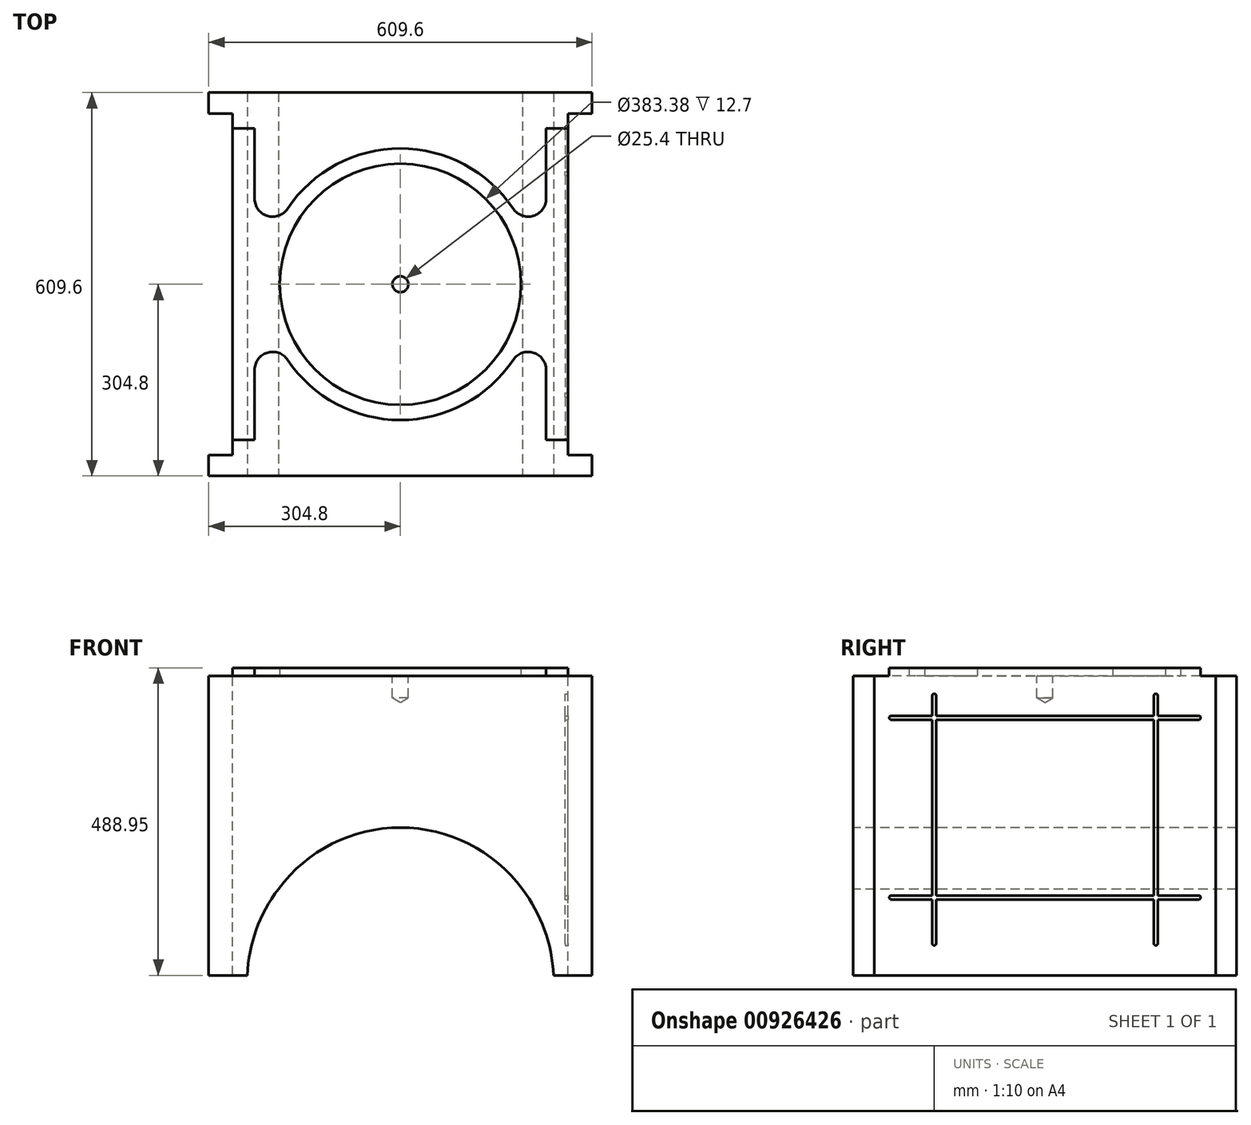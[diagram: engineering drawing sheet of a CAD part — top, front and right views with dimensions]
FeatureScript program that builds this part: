
annotation { "Feature Type Name" : "Feature", "Feature Type Description" : "" }
export const myFeature = defineFeature(function(context is Context, id is Id, definition is map)
    precondition{}
    {
        {
            var Q0;
            Q0=qCreatedBy(makeId("Top.planeOp"),FACE);
            var sketch = newSketch(context, id + "F0", { "sketchPlane" : qUnion([Q0])});
            skLineSegment(sketch, "E0.bottom", {"start": v(304.8, -304.8) * mm, "end": v(-304.8, -304.8) * mm});
            skLineSegment(sketch, "E0.top", {"start": v(304.8, 304.8) * mm, "end": v(-304.8, 304.8) * mm});
            skLineSegment(sketch, "E0.left", {"start": v(304.8, -304.8) * mm, "end": v(304.8, 304.8) * mm});
            skLineSegment(sketch, "E0.right", {"start": v(-304.8, -304.8) * mm, "end": v(-304.8, 304.8) * mm});
            skPoint(sketch, "E0.middle", {"position": v(0, 0) * mm});
            skSolve(sketch);
        }
        {
            var Q0;
            Q0=makeQuery(id+"F0.imprint","IMPRINT",FACE,{"disambiguationData":[TD([[makeQuery(id+"F0.imprint","IMPRINT",EDGE,{"derivedFrom":sQuery(id+"F0.wireOp",EDGE,"E0.bottom")}),-1.0]])]});
            extrude(context, id + "F1", {"entities" : qUnion([Q0]), "endBound" : BoundingType.SYMMETRIC, "depth" : 476.25 * mm, "offsetDistance" : 25.4 * mm});
        }
        {
            var Q0;
            Q0=makeQuery(id+"F1.opExtrude","SWEPT_FACE",FACE,{"disambiguationData":[OSD([sQuery(id+"F0.wireOp",EDGE,"E0.bottom")])]});
            var sketch = newSketch(context, id + "F2", { "sketchPlane" : qUnion([Q0])});
            skLineSegment(sketch, "E1.0", {"start": v(304.8, -238.13) * mm, "end": v(-304.8, -238.13) * mm, "construction": true});
            skLineSegment(sketch, "E2", {"start": v(-304.8, -244.48) * mm, "end": v(304.8, -244.47) * mm, "construction": true});
            skLineSegment(sketch, "E3.0", {"start": v(-243.68, -248.44) * mm, "end": v(243.68, -248.44) * mm});
            skArc(sketch, "E4", {"start": v(-193.99, -100.96) * mm, "mid": v(-230.92, -170.63) * mm, "end": v(-243.68, -248.44) * mm});
            skArc(sketch, "E5.trimOffspring", {"start": v(193.99, -100.96) * mm, "mid": v(0, -3.18) * mm, "end": v(-193.99, -100.96) * mm});
            skArc(sketch, "E6.trimOffspring", {"start": v(243.68, -248.44) * mm, "mid": v(230.92, -170.63) * mm, "end": v(193.99, -100.96) * mm});
            skPoint(sketch, "E7.orphan", {"position": v(-304.8, -248.44) * mm});
            skPoint(sketch, "E8.orphan", {"position": v(304.8, -248.44) * mm});
            skSolve(sketch);
        }
        {
            var Q0;
            Q0 = qSketchRegion(id + "F2", true);
            extrude(context, id + "F3", {"entities" : qUnion([Q0]), "operationType" : NewBodyOperationType.REMOVE, "endBound" : BoundingType.THROUGH_ALL, "oppositeDirection" : true, "depth" : 25.4 * mm, "offsetDistance" : 25.4 * mm});
        }
        {
            var Q0;
            Q0=makeQuery(id+"F1.opExtrude","CAP_FACE",FACE,{"disambiguationData":[OSD([sQuery(id+"F0.wireOp",EDGE,"E0.bottom"),sQuery(id+"F0.wireOp",EDGE,"E0.top"),sQuery(id+"F0.wireOp",EDGE,"E0.left"),sQuery(id+"F0.wireOp",EDGE,"E0.right")])],"isStart":false});
            var sketch = newSketch(context, id + "F4", { "sketchPlane" : qUnion([Q0])});
            skLineSegment(sketch, "E9.bottom", {"start": v(342.9, 271.46) * mm, "end": v(266.7, 271.46) * mm});
            skLineSegment(sketch, "E9.top", {"start": v(342.9, -271.46) * mm, "end": v(266.7, -271.46) * mm});
            skLineSegment(sketch, "E9.left", {"start": v(342.9, 271.46) * mm, "end": v(342.9, -271.46) * mm});
            skLineSegment(sketch, "E9.right", {"start": v(266.7, 271.46) * mm, "end": v(266.7, -271.46) * mm});
            skPoint(sketch, "E9.middle", {"position": v(304.8, 0) * mm});
            skLineSegment(sketch, "E10.bottom", {"start": v(-342.9, 271.46) * mm, "end": v(-266.7, 271.46) * mm});
            skLineSegment(sketch, "E10.top", {"start": v(-342.9, -271.46) * mm, "end": v(-266.7, -271.46) * mm});
            skLineSegment(sketch, "E10.left", {"start": v(-342.9, 271.46) * mm, "end": v(-342.9, -271.46) * mm});
            skLineSegment(sketch, "E10.right", {"start": v(-266.7, 271.46) * mm, "end": v(-266.7, -271.46) * mm});
            skPoint(sketch, "E10.middle", {"position": v(-304.8, 0) * mm});
            skSolve(sketch);
        }
        {
            var Q0;
            Q0 = qSketchRegion(id + "F4", true);
            extrude(context, id + "F5", {"entities" : qUnion([Q0]), "operationType" : NewBodyOperationType.REMOVE, "endBound" : BoundingType.THROUGH_ALL, "oppositeDirection" : true, "depth" : 25.4 * mm, "offsetDistance" : 25.4 * mm});
        }
        {
            var Q0;
            Q0=makeQuery(id+"F1.opExtrude","CAP_FACE",FACE,{"disambiguationData":[OSD([sQuery(id+"F0.wireOp",EDGE,"E0.bottom"),sQuery(id+"F0.wireOp",EDGE,"E0.top"),sQuery(id+"F0.wireOp",EDGE,"E0.left"),sQuery(id+"F0.wireOp",EDGE,"E0.right")])],"isStart":false});
            var sketch = newSketch(context, id + "F6", { "sketchPlane" : qUnion([Q0])});
            skLineSegment(sketch, "E11", {"start": v(-266.7, 0) * mm, "end": v(266.7, 0) * mm, "construction": true});
            skLineSegment(sketch, "E12", {"start": v(0, 304.8) * mm, "end": v(0, -304.8) * mm, "construction": true});
            skArc(sketch, "E13", {"start": v(-179.35, -120.19) * mm, "mid": v(0, -215.9) * mm, "end": v(179.35, -120.19) * mm});
            skCircle(sketch, "E14", {"center": v(0, 0) * mm, "radius": 191.7 * mm});
            skLineSegment(sketch, "E15", {"start": v(-266.7, 247.65) * mm, "end": v(-231.78, 247.65) * mm});
            skLineSegment(sketch, "E16", {"start": v(-266.7, -247.65) * mm, "end": v(-231.78, -247.65) * mm});
            skLineSegment(sketch, "E17.0", {"start": v(-266.7, 247.65) * mm, "end": v(-266.7, -247.65) * mm});
            skLineSegment(sketch, "E18.0", {"start": v(266.7, 247.65) * mm, "end": v(266.7, -247.65) * mm});
            skLineSegment(sketch, "E19", {"start": v(-231.77, 247.65) * mm, "end": v(-231.77, 136.13) * mm});
            skLineSegment(sketch, "E20", {"start": v(231.78, 247.65) * mm, "end": v(231.78, 136.13) * mm});
            skPoint(sketch, "E21.orphan", {"position": v(-231.78, 271.46) * mm});
            skLineSegment(sketch, "E22.trimOffspring", {"start": v(231.77, 247.65) * mm, "end": v(266.7, 247.65) * mm});
            skPoint(sketch, "E23.orphan", {"position": v(231.77, 271.46) * mm});
            skPoint(sketch, "E24.orphan", {"position": v(-231.78, -271.46) * mm});
            skPoint(sketch, "E25.orphan", {"position": v(231.78, -271.46) * mm});
            skPoint(sketch, "E26.orphan", {"position": v(266.7, -271.46) * mm});
            skPoint(sketch, "E27.orphan", {"position": v(-266.7, -271.46) * mm});
            skPoint(sketch, "E28.orphan", {"position": v(-266.7, 271.46) * mm});
            skPoint(sketch, "E29.orphan", {"position": v(266.7, 271.46) * mm});
            skLineSegment(sketch, "E30.0", {"start": v(-266.7, -136.13) * mm, "end": v(266.7, -136.13) * mm, "construction": true});
            skLineSegment(sketch, "E31.MirrorCS", {"start": v(-266.7, 136.13) * mm, "end": v(266.7, 136.13) * mm, "construction": true});
            skArc(sketch, "E32", {"start": v(179.35, 120.19) * mm, "mid": v(211.47, 108.73) * mm, "end": v(231.78, 136.13) * mm});
            skArc(sketch, "E33.MirrorC", {"start": v(-179.35, 120.19) * mm, "mid": v(-211.47, 108.73) * mm, "end": v(-231.78, 136.13) * mm});
            skArc(sketch, "E34.MirrorC", {"start": v(-179.35, -120.19) * mm, "mid": v(-211.47, -108.73) * mm, "end": v(-231.78, -136.13) * mm});
            skArc(sketch, "E35.MirrorC", {"start": v(179.35, -120.19) * mm, "mid": v(211.47, -108.73) * mm, "end": v(231.78, -136.13) * mm});
            skLineSegment(sketch, "E36.trimOffspring", {"start": v(-231.78, -136.13) * mm, "end": v(-231.78, -247.65) * mm});
            skArc(sketch, "E37.trimOffspring", {"start": v(179.35, 120.19) * mm, "mid": v(0, 215.9) * mm, "end": v(-179.35, 120.19) * mm});
            skLineSegment(sketch, "E38.trimOffspring", {"start": v(231.77, -136.13) * mm, "end": v(231.77, -247.65) * mm});
            skLineSegment(sketch, "E39.trimOffspring", {"start": v(231.77, -247.65) * mm, "end": v(266.7, -247.65) * mm});
            skSolve(sketch);
        }
        {
            var Q0;
            Q0 = qSketchRegion(id + "F6", true);
            extrude(context, id + "F7", {"entities" : qUnion([Q0]), "operationType" : NewBodyOperationType.ADD, "depth" : 12.7 * mm, "offsetDistance" : 25.4 * mm});
        }
        {
            var Q0;
            Q0=makeQuery(id+"F7.boolean.opBoolean","SPLIT",FACE,{"disambiguationData":[TD([makeQuery(id+"F7.opExtrude","SWEPT_FACE",FACE,{"disambiguationData":[OSD([sQuery(id+"F6.wireOp",EDGE,"E14")])]})])],"derivedFrom":makeQuery(id+"F1.opExtrude","CAP_FACE",FACE,{"disambiguationData":[OSD([sQuery(id+"F0.wireOp",EDGE,"E0.bottom"),sQuery(id+"F0.wireOp",EDGE,"E0.top"),sQuery(id+"F0.wireOp",EDGE,"E0.left"),sQuery(id+"F0.wireOp",EDGE,"E0.right")])],"isStart":false})});
            var sketch = newSketch(context, id + "F8", { "sketchPlane" : qUnion([Q0])});
            skCircle(sketch, "E40.0", {"center": v(0, 0) * mm, "radius": 191.7 * mm, "construction": true});
            skSolve(sketch);
        }
        {
            var Q0;
            Q0=sQuery(id+"F8.wireOp",VERTEX,"E40.0.center");
            var Q1;
            Q1=makeQuery(id+"F1.opExtrude","SWEPT_BODY",BODY,{"disambiguationData":[OSD([sQuery(id+"F0.wireOp",EDGE,"E0.bottom"),sQuery(id+"F0.wireOp",EDGE,"E0.top"),sQuery(id+"F0.wireOp",EDGE,"E0.left"),sQuery(id+"F0.wireOp",EDGE,"E0.right")])]});
            hole(context, id + "F9", {"style" : HoleStyle.SIMPLE, "endStyle" : HoleEndStyle.BLIND, "standardTappedOrClearance" : lookupTablePath({ "standard" : "ANSI", "size" : "1 (1)", "type" : "Drilled" }), "standardBlindInLast" : lookupTablePath({ "standard" : "ANSI", "size" : "1", "type" : "Drilled" }), "holeDiameter" : 25.4 * mm, "majorDiameter" : 6.35 * mm, "holeDepth" : 34.92 * mm, "isTappedThrough" : true, "tappedDepth" : 12.7 * mm, "tapClearance" : 3, "startFromSketch" : true, "locations" : qUnion([Q0]), "scope" : qUnion([Q1])});
        }
        {
            var Q0;
            Q0=makeQuery(id+"F7.boolean.opBoolean","MERGE",FACE,{"derivedFrom":[makeQuery(id+"F5.boolean.opBoolean","COPY",FACE,{"derivedFrom":makeQuery(id+"F5.opExtrude","SWEPT_FACE",FACE,{"disambiguationData":[OSD([sQuery(id+"F4.wireOp",EDGE,"E9.right")])]})}),makeQuery(id+"F7.opExtrude","SWEPT_FACE",FACE,{"disambiguationData":[OSD([sQuery(id+"F6.wireOp",EDGE,"E18.0")])]})]});
            var sketch = newSketch(context, id + "F10", { "sketchPlane" : qUnion([Q0])});
            skLineSegment(sketch, "E41.bottom", {"start": v(244.47, -117.47) * mm, "end": v(179.39, -117.47) * mm});
            skLineSegment(sketch, "E41.top", {"start": v(244.47, -111.12) * mm, "end": v(179.39, -111.12) * mm});
            skLineSegment(sketch, "E42", {"start": v(0, -238.13) * mm, "end": v(0, 250.83) * mm, "construction": true});
            skLineSegment(sketch, "E43.left", {"start": v(179.39, -187.32) * mm, "end": v(179.39, -117.47) * mm});
            skLineSegment(sketch, "E43.right", {"start": v(173.04, -187.32) * mm, "end": v(173.04, -117.47) * mm});
            skArc(sketch, "E44", {"start": v(173.04, -187.32) * mm, "mid": v(176.21, -190.5) * mm, "end": v(179.39, -187.32) * mm});
            skArc(sketch, "E45", {"start": v(244.47, -117.48) * mm, "mid": v(247.65, -114.3) * mm, "end": v(244.47, -111.12) * mm});
            skArc(sketch, "E46", {"start": v(-244.47, -111.12) * mm, "mid": v(-247.65, -114.3) * mm, "end": v(-244.47, -117.47) * mm});
            skArc(sketch, "E47", {"start": v(179.39, 206.37) * mm, "mid": v(176.21, 209.55) * mm, "end": v(173.04, 206.37) * mm});
            skLineSegment(sketch, "E48.0.1.0", {"start": v(244.47, 174.62) * mm, "end": v(179.39, 174.62) * mm});
            skLineSegment(sketch, "E48.0.1.1", {"start": v(244.47, 168.28) * mm, "end": v(179.39, 168.28) * mm});
            skArc(sketch, "E48.0.1.2", {"start": v(244.47, 168.28) * mm, "mid": v(247.65, 171.45) * mm, "end": v(244.47, 174.63) * mm});
            skArc(sketch, "E48.0.1.3", {"start": v(-244.47, 174.63) * mm, "mid": v(-247.65, 171.45) * mm, "end": v(-244.47, 168.28) * mm});
            skLineSegment(sketch, "E48.direction1", {"start": v(-244.47, -117.48) * mm, "end": v(-222.8, -117.48) * mm, "construction": true});
            skLineSegment(sketch, "E48.direction2", {"start": v(-244.47, -117.47) * mm, "end": v(-244.47, 168.28) * mm, "construction": true});
            skArc(sketch, "E49.MirrorCS", {"start": v(-179.39, 206.37) * mm, "mid": v(-176.21, 209.55) * mm, "end": v(-173.04, 206.37) * mm});
            skArc(sketch, "E50.MirrorCS", {"start": v(-173.04, -187.32) * mm, "mid": v(-176.21, -190.5) * mm, "end": v(-179.39, -187.32) * mm});
            skLineSegment(sketch, "E51.MirrorCS", {"start": v(-173.04, -187.32) * mm, "end": v(-173.04, -117.48) * mm});
            skLineSegment(sketch, "E52.MirrorCS", {"start": v(-179.39, -187.32) * mm, "end": v(-179.39, -117.48) * mm});
            skLineSegment(sketch, "E53.trimOffspring", {"start": v(173.04, -111.12) * mm, "end": v(173.04, 168.28) * mm});
            skLineSegment(sketch, "E54.trimOffspring", {"start": v(173.04, -117.47) * mm, "end": v(-173.04, -117.48) * mm});
            skLineSegment(sketch, "E55.trimOffspring", {"start": v(179.39, -111.12) * mm, "end": v(179.39, 168.28) * mm});
            skLineSegment(sketch, "E56.trimOffspring", {"start": v(173.04, -111.12) * mm, "end": v(-173.04, -111.13) * mm});
            skLineSegment(sketch, "E57.trimOffspring", {"start": v(-179.39, -111.13) * mm, "end": v(-179.39, 168.28) * mm});
            skLineSegment(sketch, "E58.trimOffspring", {"start": v(-179.39, -117.48) * mm, "end": v(-244.47, -117.48) * mm});
            skLineSegment(sketch, "E59.trimOffspring", {"start": v(-173.04, -111.13) * mm, "end": v(-173.04, 168.28) * mm});
            skLineSegment(sketch, "E60.trimOffspring", {"start": v(-179.39, -111.13) * mm, "end": v(-244.47, -111.13) * mm});
            skLineSegment(sketch, "E61.trimOffspring", {"start": v(-179.39, 174.62) * mm, "end": v(-179.39, 206.37) * mm});
            skLineSegment(sketch, "E62.trimOffspring", {"start": v(-179.39, 168.28) * mm, "end": v(-244.47, 168.28) * mm});
            skLineSegment(sketch, "E63.trimOffspring", {"start": v(-173.04, 174.62) * mm, "end": v(-173.04, 206.37) * mm});
            skLineSegment(sketch, "E64.trimOffspring", {"start": v(-179.39, 174.62) * mm, "end": v(-244.47, 174.62) * mm});
            skLineSegment(sketch, "E65.trimOffspring", {"start": v(173.04, 174.62) * mm, "end": v(173.04, 206.37) * mm});
            skLineSegment(sketch, "E66.trimOffspring", {"start": v(173.04, 168.28) * mm, "end": v(-173.04, 168.28) * mm});
            skLineSegment(sketch, "E67.trimOffspring", {"start": v(173.04, 174.62) * mm, "end": v(-173.04, 174.62) * mm});
            skLineSegment(sketch, "E68.trimOffspring", {"start": v(179.39, 174.63) * mm, "end": v(179.39, 206.37) * mm});
            skSolve(sketch);
        }
        {
            var Q0;
            Q0 = qSketchRegion(id + "F10", true);
            extrude(context, id + "F11", {"entities" : qUnion([Q0]), "operationType" : NewBodyOperationType.REMOVE, "oppositeDirection" : true, "depth" : 4.76 * mm, "offsetDistance" : 25.4 * mm});
        }
    });
